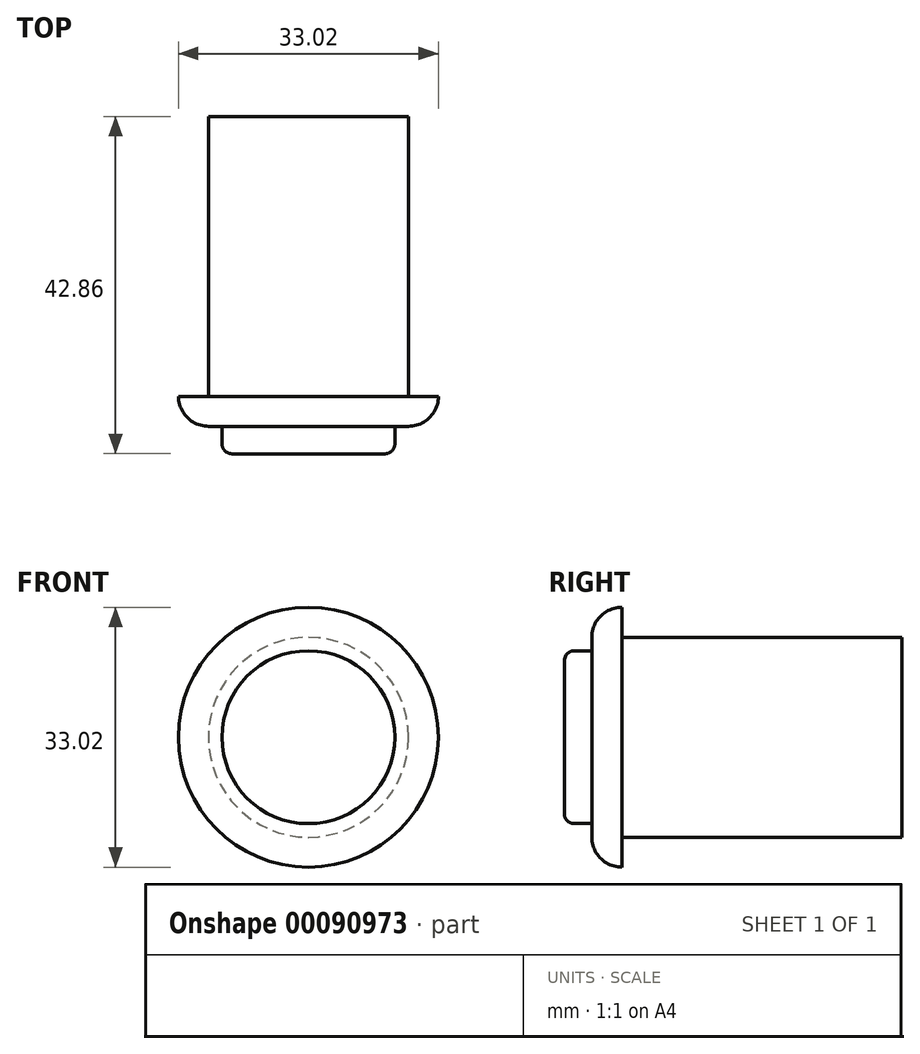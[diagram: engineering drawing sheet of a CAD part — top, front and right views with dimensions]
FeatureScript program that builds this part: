
annotation { "Feature Type Name" : "Feature", "Feature Type Description" : "" }
export const myFeature = defineFeature(function(context is Context, id is Id, definition is map)
    precondition{}
    {
        {
            var Q0;
            Q0=qCreatedBy(makeId("Right.planeOp"),FACE);
            var sketch = newSketch(context, id + "F0", { "sketchPlane" : qUnion([Q0])});
            skArc(sketch, "E0", {"start": v(0, 16.5) * mm, "mid": v(-2.7, 15.4) * mm, "end": v(-3.8, 12.7) * mm});
            skLineSegment(sketch, "E1", {"start": v(-3.8, 12.7) * mm, "end": v(-3.8, 10.98) * mm});
            skLineSegment(sketch, "E2", {"start": v(-3.81, 10.98) * mm, "end": v(-6.03, 10.98) * mm});
            skArc(sketch, "E3", {"start": v(-6.03, 10.98) * mm, "mid": v(-6.93, 10.6) * mm, "end": v(-7.3, 9.7) * mm});
            skLineSegment(sketch, "E4", {"start": v(-7.3, 9.7) * mm, "end": v(-7.3, 0) * mm});
            skLineSegment(sketch, "E5", {"start": v(-7.3, 0) * mm, "end": v(0, 0) * mm});
            skLineSegment(sketch, "E6", {"start": v(0, 0) * mm, "end": v(35.56, 0) * mm});
            skLineSegment(sketch, "E7", {"start": v(35.56, 0) * mm, "end": v(35.56, 12.7) * mm});
            skLineSegment(sketch, "E8", {"start": v(35.56, 12.7) * mm, "end": v(0, 12.7) * mm});
            skLineSegment(sketch, "E9", {"start": v(0, 12.7) * mm, "end": v(0, 16.51) * mm});
            skSolve(sketch);
        }
        {
            var Q0;
            Q0=makeQuery(id+"F0.imprint","IMPRINT",FACE,{"disambiguationData":[TD([[makeQuery(id+"F0.imprint","IMPRINT",EDGE,{"derivedFrom":sQuery(id+"F0.wireOp",EDGE,"E0")}),1.0]])]});
            var Q1;
            Q1=sQuery(id+"F0.wireOp",EDGE,"E6");
            revolve(context, id + "F1", {"entities" : qUnion([Q0]), "axis" : qUnion([Q1]), "revolveType" : RevolveType.FULL});
        }
    });
